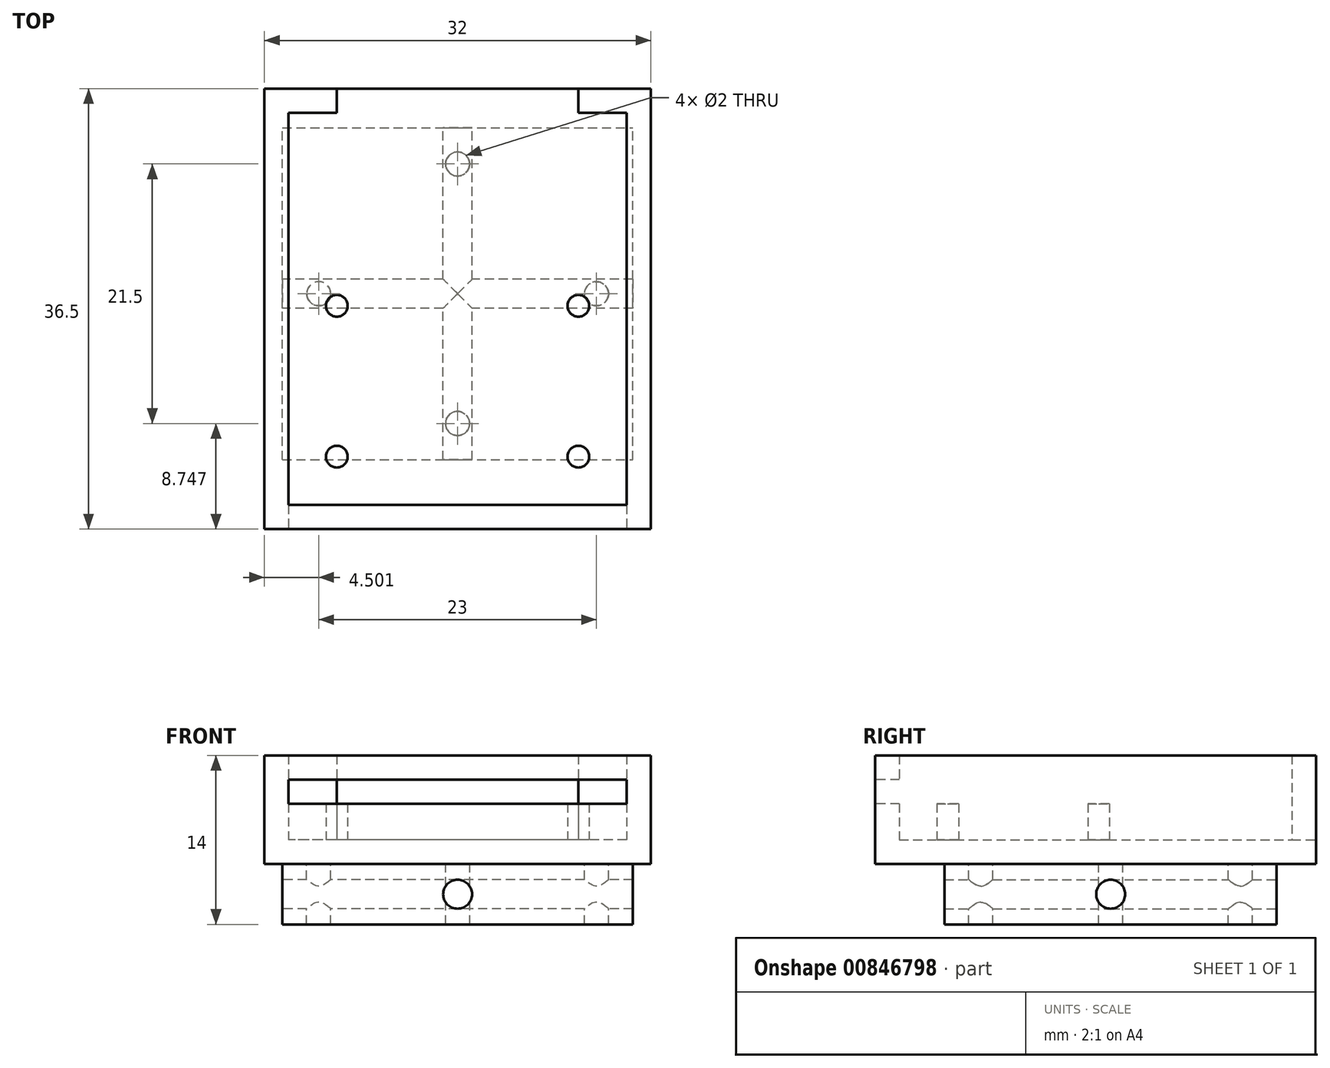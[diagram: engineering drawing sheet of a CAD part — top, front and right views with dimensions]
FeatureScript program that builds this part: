
annotation { "Feature Type Name" : "Feature", "Feature Type Description" : "" }
export const myFeature = defineFeature(function(context is Context, id is Id, definition is map)
    precondition{}
    {
        {
            var Q0;
            Q0=qCreatedBy(makeId("Top.planeOp"),FACE);
            var sketch = newSketch(context, id + "F0", { "sketchPlane" : qUnion([Q0])});
            skLineSegment(sketch, "E0.bottom", {"start": v(-84.2, 28.98) * mm, "end": v(-112.2, 28.98) * mm});
            skLineSegment(sketch, "E0.top", {"start": v(-84.2, 61.48) * mm, "end": v(-112.2, 61.48) * mm});
            skLineSegment(sketch, "E0.left", {"start": v(-84.2, 28.98) * mm, "end": v(-84.2, 61.48) * mm});
            skLineSegment(sketch, "E0.right", {"start": v(-112.2, 28.98) * mm, "end": v(-112.2, 61.48) * mm});
            skPoint(sketch, "E0.middle", {"position": v(-98.2, 45.23) * mm});
            skCircle(sketch, "E1", {"center": v(-108.2, 32.98) * mm, "radius": 0.9 * mm});
            skCircle(sketch, "E2", {"center": v(-108.2, 45.48) * mm, "radius": 0.9 * mm});
            skCircle(sketch, "E3", {"center": v(-88.2, 45.48) * mm, "radius": 0.9 * mm});
            skCircle(sketch, "E4", {"center": v(-88.2, 32.98) * mm, "radius": 0.9 * mm});
            skLineSegment(sketch, "E5.bottom", {"start": v(-114.2, 63.48) * mm, "end": v(-82.2, 63.48) * mm});
            skLineSegment(sketch, "E5.top", {"start": v(-114.2, 26.98) * mm, "end": v(-82.2, 26.98) * mm});
            skLineSegment(sketch, "E5.left", {"start": v(-114.2, 63.48) * mm, "end": v(-114.2, 26.98) * mm});
            skLineSegment(sketch, "E5.right", {"start": v(-82.2, 63.48) * mm, "end": v(-82.2, 26.98) * mm});
            skSolve(sketch);
        }
        {
            var Q0;
            Q0=makeQuery(id+"F0.imprint","IMPRINT",FACE,{"disambiguationData":[TD([[makeQuery(id+"F0.imprint","IMPRINT",EDGE,{"derivedFrom":sQuery(id+"F0.wireOp",EDGE,"E0.bottom")}),1.0]])]});
            extrude(context, id + "F1", {"entities" : qUnion([Q0]), "depth" : 9 * mm, "offsetDistance" : 25 * mm});
        }
        {
            var Q0;
            Q0=makeQuery(id+"F0.imprint","IMPRINT",FACE,{"disambiguationData":[TD([[makeQuery(id+"F0.imprint","IMPRINT",EDGE,{"derivedFrom":sQuery(id+"F0.wireOp",EDGE,"E0.bottom")}),-1.0]])]});
            extrude(context, id + "F2", {"entities" : qUnion([Q0]), "operationType" : NewBodyOperationType.ADD, "depth" : 2 * mm, "offsetDistance" : 25 * mm});
        }
        {
            var Q0;
            Q0=makeQuery(id+"F0.imprint","IMPRINT",FACE,{"disambiguationData":[TD([[makeQuery(id+"F0.imprint","IMPRINT",EDGE,{"derivedFrom":sQuery(id+"F0.wireOp",EDGE,"E1")}),1.0]])]});
            var Q1;
            Q1=makeQuery(id+"F0.imprint","IMPRINT",FACE,{"disambiguationData":[TD([[makeQuery(id+"F0.imprint","IMPRINT",EDGE,{"derivedFrom":sQuery(id+"F0.wireOp",EDGE,"E2")}),1.0]])]});
            var Q2;
            Q2=makeQuery(id+"F0.imprint","IMPRINT",FACE,{"disambiguationData":[TD([[makeQuery(id+"F0.imprint","IMPRINT",EDGE,{"derivedFrom":sQuery(id+"F0.wireOp",EDGE,"E4")}),1.0]])]});
            var Q3;
            Q3=makeQuery(id+"F0.imprint","IMPRINT",FACE,{"disambiguationData":[TD([[makeQuery(id+"F0.imprint","IMPRINT",EDGE,{"derivedFrom":sQuery(id+"F0.wireOp",EDGE,"E3")}),1.0]])]});
            extrude(context, id + "F3", {"entities" : qUnion([Q0, Q1, Q2, Q3]), "operationType" : NewBodyOperationType.ADD, "depth" : 5 * mm, "offsetDistance" : 25 * mm});
        }
        {
            var Q0;
            Q0=makeQuery(id+"F1.opExtrude","SWEPT_FACE",FACE,{"disambiguationData":[OSD([sQuery(id+"F0.wireOp",EDGE,"E5.top")])]});
            var sketch = newSketch(context, id + "F4", { "sketchPlane" : qUnion([Q0])});
            skLineSegment(sketch, "E6.bottom", {"start": v(-112.2, 7) * mm, "end": v(-84.2, 7) * mm});
            skLineSegment(sketch, "E6.top", {"start": v(-112.2, 5) * mm, "end": v(-84.2, 5) * mm});
            skLineSegment(sketch, "E6.left", {"start": v(-112.2, 7) * mm, "end": v(-112.2, 5) * mm});
            skLineSegment(sketch, "E6.right", {"start": v(-84.2, 7) * mm, "end": v(-84.2, 5) * mm});
            skSolve(sketch);
        }
        {
            var Q0;
            Q0=makeQuery(id+"F4.imprint","IMPRINT",FACE,{"disambiguationData":[TD([[makeQuery(id+"F4.imprint","IMPRINT",EDGE,{"derivedFrom":sQuery(id+"F4.wireOp",EDGE,"E6.bottom")}),-1.0]])]});
            extrude(context, id + "F5", {"entities" : qUnion([Q0]), "operationType" : NewBodyOperationType.REMOVE, "endBound" : BoundingType.UP_TO_NEXT, "oppositeDirection" : true, "depth" : 25 * mm, "offsetDistance" : 25 * mm});
        }
        {
            var Q0;
            Q0=makeQuery(id+"F1.opExtrude","SWEPT_FACE",FACE,{"disambiguationData":[OSD([sQuery(id+"F0.wireOp",EDGE,"E5.bottom")])]});
            var sketch = newSketch(context, id + "F6", { "sketchPlane" : qUnion([Q0])});
            skLineSegment(sketch, "E7.bottom", {"start": v(88.2, 9) * mm, "end": v(108.2, 9) * mm});
            skLineSegment(sketch, "E7.top", {"start": v(88.2, 2) * mm, "end": v(108.2, 2) * mm});
            skLineSegment(sketch, "E7.left", {"start": v(88.2, 9) * mm, "end": v(88.2, 2) * mm});
            skLineSegment(sketch, "E7.right", {"start": v(108.2, 9) * mm, "end": v(108.2, 2) * mm});
            skSolve(sketch);
        }
        {
            var Q0;
            Q0=makeQuery(id+"F6.imprint","IMPRINT",FACE,{"disambiguationData":[TD([[makeQuery(id+"F6.imprint","IMPRINT",EDGE,{"derivedFrom":sQuery(id+"F6.wireOp",EDGE,"E7.bottom")}),1.0]])]});
            extrude(context, id + "F7", {"entities" : qUnion([Q0]), "operationType" : NewBodyOperationType.REMOVE, "endBound" : BoundingType.UP_TO_NEXT, "oppositeDirection" : true, "depth" : 25 * mm, "offsetDistance" : 25 * mm});
        }
        {
            var Q0;
            {var subQ0=sQuery(id+"F0.wireOp",EDGE,"E4");var subQ1=sQuery(id+"F0.wireOp",EDGE,"E3");var subQ2=sQuery(id+"F0.wireOp",EDGE,"E2");var subQ3=sQuery(id+"F0.wireOp",EDGE,"E1");var subQ4=sQuery(id+"F0.wireOp",EDGE,"E0.right");var subQ5=sQuery(id+"F0.wireOp",EDGE,"E0.left");var subQ6=sQuery(id+"F0.wireOp",EDGE,"E0.top");var subQ7=sQuery(id+"F0.wireOp",EDGE,"E0.bottom");Q0=makeQuery(id+"F3.boolean.opBoolean","MERGE",FACE,{"derivedFrom":[makeQuery(id+"F2.boolean.opBoolean","MERGE",FACE,{"derivedFrom":[makeQuery(id+"F1.opExtrude","CAP_FACE",FACE,{"disambiguationData":[OSD([subQ7,subQ6,subQ5,subQ4,sQuery(id+"F0.wireOp",EDGE,"E5.bottom"),sQuery(id+"F0.wireOp",EDGE,"E5.top"),sQuery(id+"F0.wireOp",EDGE,"E5.left"),sQuery(id+"F0.wireOp",EDGE,"E5.right")])],"isStart":true}),makeQuery(id+"F2.opExtrude","CAP_FACE",FACE,{"disambiguationData":[OSD([subQ7,subQ6,subQ5,subQ4,subQ3,subQ2,subQ1,subQ0])],"isStart":true})]}),makeQuery(id+"F3.opExtrude","CAP_FACE",FACE,{"disambiguationData":[OSD([subQ3])],"isStart":true}),makeQuery(id+"F3.opExtrude","CAP_FACE",FACE,{"disambiguationData":[OSD([subQ2])],"isStart":true}),makeQuery(id+"F3.opExtrude","CAP_FACE",FACE,{"disambiguationData":[OSD([subQ1])],"isStart":true}),makeQuery(id+"F3.opExtrude","CAP_FACE",FACE,{"disambiguationData":[OSD([subQ0])],"isStart":true})]});}
            var sketch = newSketch(context, id + "F8", { "sketchPlane" : qUnion([Q0])});
            skLineSegment(sketch, "E8.bottom", {"start": v(-82.2, -63.48) * mm, "end": v(-114.2, -63.48) * mm});
            skLineSegment(sketch, "E8.top", {"start": v(-82.2, -26.98) * mm, "end": v(-114.2, -26.98) * mm});
            skLineSegment(sketch, "E8.left", {"start": v(-82.2, -63.48) * mm, "end": v(-82.2, -26.98) * mm});
            skLineSegment(sketch, "E8.right", {"start": v(-114.2, -63.48) * mm, "end": v(-114.2, -26.98) * mm});
            skLineSegment(sketch, "E9.bottom", {"start": v(-112.7, -32.73) * mm, "end": v(-83.7, -32.73) * mm});
            skLineSegment(sketch, "E9.top", {"start": v(-112.7, -60.23) * mm, "end": v(-83.7, -60.23) * mm});
            skLineSegment(sketch, "E9.left", {"start": v(-112.7, -32.73) * mm, "end": v(-112.7, -60.23) * mm});
            skLineSegment(sketch, "E9.right", {"start": v(-83.7, -32.73) * mm, "end": v(-83.7, -60.23) * mm});
            skPoint(sketch, "E9.middle", {"position": v(-98.2, -46.48) * mm});
            skLineSegment(sketch, "E10.bottom", {"start": v(-109.7, -35.73) * mm, "end": v(-86.7, -35.73) * mm});
            skLineSegment(sketch, "E10.top", {"start": v(-109.7, -57.23) * mm, "end": v(-86.7, -57.23) * mm});
            skLineSegment(sketch, "E10.left", {"start": v(-109.7, -35.73) * mm, "end": v(-109.7, -57.23) * mm});
            skLineSegment(sketch, "E10.right", {"start": v(-86.7, -35.73) * mm, "end": v(-86.7, -57.23) * mm});
            skCircle(sketch, "E11", {"center": v(-86.7, -46.48) * mm, "radius": 1 * mm});
            skCircle(sketch, "E12", {"center": v(-109.7, -46.48) * mm, "radius": 1 * mm});
            skCircle(sketch, "E13", {"center": v(-98.2, -35.73) * mm, "radius": 1 * mm});
            skCircle(sketch, "E14", {"center": v(-98.2, -57.23) * mm, "radius": 1 * mm});
            skSolve(sketch);
        }
        {
            var Q0;
            Q0=makeQuery(id+"F8.imprint","IMPRINT",FACE,{"disambiguationData":[TD([[makeQuery(id+"F8.imprint","IMPRINT",EDGE,{"derivedFrom":sQuery(id+"F8.wireOp",EDGE,"E9.bottom")}),-1.0]])]});
            var Q1;
            {var subQ0=sQuery(id+"F8.wireOp",EDGE,"E11");var subQ1=sQuery(id+"F8.wireOp",EDGE,"E10.right");var subQ2=makeQuery(id+"F8.imprint","INTERSECT",VERTEX,{"disambiguationData":[OD(0.0)],"derivedFrom":[subQ1,subQ0]});Q1=makeQuery(id+"F8.imprint","IMPRINT",FACE,{"disambiguationData":[TD([[makeQuery(id+"F8.imprint","IMPRINT",EDGE,{"disambiguationData":[TD([[subQ2,-1.0]])],"derivedFrom":subQ1}),-1.0]])]});}
            var Q2;
            {var subQ0=sQuery(id+"F8.wireOp",EDGE,"E11");var subQ1=sQuery(id+"F8.wireOp",EDGE,"E10.right");var subQ2=makeQuery(id+"F8.imprint","INTERSECT",VERTEX,{"disambiguationData":[OD(0.0)],"derivedFrom":[subQ1,subQ0]});Q2=makeQuery(id+"F8.imprint","IMPRINT",FACE,{"disambiguationData":[TD([[makeQuery(id+"F8.imprint","IMPRINT",EDGE,{"disambiguationData":[TD([[subQ2,-1.0]])],"derivedFrom":subQ1}),1.0]])]});}
            var Q3;
            {var subQ0=sQuery(id+"F8.wireOp",EDGE,"E13");var subQ1=sQuery(id+"F8.wireOp",EDGE,"E10.bottom");var subQ2=makeQuery(id+"F8.imprint","INTERSECT",VERTEX,{"disambiguationData":[OD(0.0)],"derivedFrom":[subQ1,subQ0]});Q3=makeQuery(id+"F8.imprint","IMPRINT",FACE,{"disambiguationData":[TD([[makeQuery(id+"F8.imprint","IMPRINT",EDGE,{"disambiguationData":[TD([[subQ2,-1.0]])],"derivedFrom":subQ1}),1.0]])]});}
            var Q4;
            {var subQ0=sQuery(id+"F8.wireOp",EDGE,"E13");var subQ1=sQuery(id+"F8.wireOp",EDGE,"E10.bottom");var subQ2=makeQuery(id+"F8.imprint","INTERSECT",VERTEX,{"disambiguationData":[OD(0.0)],"derivedFrom":[subQ1,subQ0]});Q4=makeQuery(id+"F8.imprint","IMPRINT",FACE,{"disambiguationData":[TD([[makeQuery(id+"F8.imprint","IMPRINT",EDGE,{"disambiguationData":[TD([[subQ2,-1.0]])],"derivedFrom":subQ1}),-1.0]])]});}
            var Q5;
            {var subQ0=sQuery(id+"F8.wireOp",EDGE,"E12");var subQ1=sQuery(id+"F8.wireOp",EDGE,"E10.left");var subQ2=makeQuery(id+"F8.imprint","INTERSECT",VERTEX,{"disambiguationData":[OD(0.0)],"derivedFrom":[subQ1,subQ0]});Q5=makeQuery(id+"F8.imprint","IMPRINT",FACE,{"disambiguationData":[TD([[makeQuery(id+"F8.imprint","IMPRINT",EDGE,{"disambiguationData":[TD([[subQ2,-1.0]])],"derivedFrom":subQ1}),1.0]])]});}
            var Q6;
            {var subQ0=sQuery(id+"F8.wireOp",EDGE,"E12");var subQ1=sQuery(id+"F8.wireOp",EDGE,"E10.left");var subQ2=makeQuery(id+"F8.imprint","INTERSECT",VERTEX,{"disambiguationData":[OD(0.0)],"derivedFrom":[subQ1,subQ0]});Q6=makeQuery(id+"F8.imprint","IMPRINT",FACE,{"disambiguationData":[TD([[makeQuery(id+"F8.imprint","IMPRINT",EDGE,{"disambiguationData":[TD([[subQ2,-1.0]])],"derivedFrom":subQ1}),-1.0]])]});}
            var Q7;
            {var subQ0=sQuery(id+"F8.wireOp",EDGE,"E14");var subQ1=sQuery(id+"F8.wireOp",EDGE,"E10.top");var subQ2=makeQuery(id+"F8.imprint","INTERSECT",VERTEX,{"disambiguationData":[OD(0.0)],"derivedFrom":[subQ1,subQ0]});Q7=makeQuery(id+"F8.imprint","IMPRINT",FACE,{"disambiguationData":[TD([[makeQuery(id+"F8.imprint","IMPRINT",EDGE,{"disambiguationData":[TD([[subQ2,-1.0]])],"derivedFrom":subQ1}),1.0]])]});}
            var Q8;
            {var subQ0=sQuery(id+"F8.wireOp",EDGE,"E14");var subQ1=sQuery(id+"F8.wireOp",EDGE,"E10.top");var subQ2=makeQuery(id+"F8.imprint","INTERSECT",VERTEX,{"disambiguationData":[OD(0.0)],"derivedFrom":[subQ1,subQ0]});Q8=makeQuery(id+"F8.imprint","IMPRINT",FACE,{"disambiguationData":[TD([[makeQuery(id+"F8.imprint","IMPRINT",EDGE,{"disambiguationData":[TD([[subQ2,-1.0]])],"derivedFrom":subQ1}),-1.0]])]});}
            extrude(context, id + "F9", {"entities" : qUnion([Q0, Q1, Q2, Q3, Q4, Q5, Q6, Q7, Q8]), "operationType" : NewBodyOperationType.ADD, "depth" : 5 * mm, "offsetDistance" : 25 * mm});
        }
        {
            var Q0;
            Q0=makeQuery(id+"F9.opExtrude","SWEPT_FACE",FACE,{"disambiguationData":[OSD([sQuery(id+"F8.wireOp",EDGE,"E9.top")])]});
            var sketch = newSketch(context, id + "F10", { "sketchPlane" : qUnion([Q0])});
            skPoint(sketch, "E15", {"position": v(98.2, -2.5) * mm});
            skPoint(sketch, "E15.positionSnap0", {"position": v(98.2, -5) * mm});
            skPoint(sketch, "E15.positionSnap1", {"position": v(83.7, -2.5) * mm});
            skSolve(sketch);
        }
        {
            var Q0;
            Q0=sQuery(id+"F10.wireOp",VERTEX,"E15");
            var Q1;
            Q1=makeQuery(id+"F1.opExtrude","SWEPT_BODY",BODY,{"disambiguationData":[OSD([sQuery(id+"F0.wireOp",EDGE,"E0.bottom"),sQuery(id+"F0.wireOp",EDGE,"E0.top"),sQuery(id+"F0.wireOp",EDGE,"E0.left"),sQuery(id+"F0.wireOp",EDGE,"E0.right"),sQuery(id+"F0.wireOp",EDGE,"E5.bottom"),sQuery(id+"F0.wireOp",EDGE,"E5.top"),sQuery(id+"F0.wireOp",EDGE,"E5.left"),sQuery(id+"F0.wireOp",EDGE,"E5.right")])]});
            hole(context, id + "F11", {"style" : HoleStyle.SIMPLE, "endStyle" : HoleEndStyle.THROUGH, "holeDiameter" : 2.4 * mm, "majorDiameter" : 5 * mm, "isTappedThrough" : true, "tappedDepth" : 12 * mm, "tapClearance" : 3, "locations" : qUnion([Q0]), "scope" : qUnion([Q1])});
        }
        {
            var Q0;
            Q0=makeQuery(id+"F9.opExtrude","SWEPT_FACE",FACE,{"disambiguationData":[OSD([sQuery(id+"F8.wireOp",EDGE,"E9.left")])]});
            var sketch = newSketch(context, id + "F12", { "sketchPlane" : qUnion([Q0])});
            skPoint(sketch, "E16", {"position": v(-46.48, -2.5) * mm});
            skPoint(sketch, "E16.positionSnap0", {"position": v(-46.48, -5) * mm});
            skPoint(sketch, "E16.positionSnap1", {"position": v(-60.23, -2.5) * mm});
            skSolve(sketch);
        }
        {
            var Q0;
            Q0=sQuery(id+"F12.wireOp",VERTEX,"E16");
            var Q1;
            Q1=makeQuery(id+"F1.opExtrude","SWEPT_BODY",BODY,{"disambiguationData":[OSD([sQuery(id+"F0.wireOp",EDGE,"E0.bottom"),sQuery(id+"F0.wireOp",EDGE,"E0.top"),sQuery(id+"F0.wireOp",EDGE,"E0.left"),sQuery(id+"F0.wireOp",EDGE,"E0.right"),sQuery(id+"F0.wireOp",EDGE,"E5.bottom"),sQuery(id+"F0.wireOp",EDGE,"E5.top"),sQuery(id+"F0.wireOp",EDGE,"E5.left"),sQuery(id+"F0.wireOp",EDGE,"E5.right")])]});
            hole(context, id + "F13", {"style" : HoleStyle.SIMPLE, "endStyle" : HoleEndStyle.THROUGH, "holeDiameter" : 2.4 * mm, "majorDiameter" : 5 * mm, "isTappedThrough" : true, "tappedDepth" : 12 * mm, "tapClearance" : 3, "locations" : qUnion([Q0]), "scope" : qUnion([Q1])});
        }
    });
